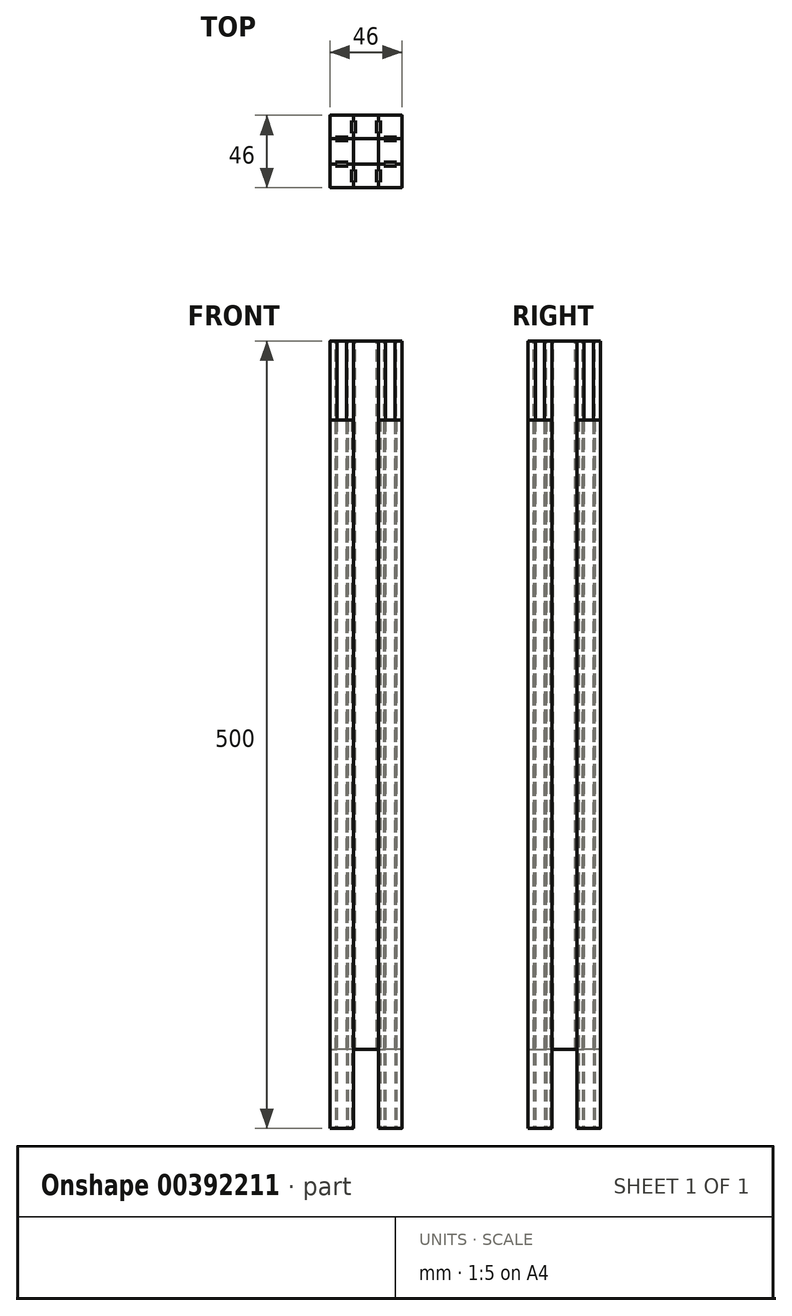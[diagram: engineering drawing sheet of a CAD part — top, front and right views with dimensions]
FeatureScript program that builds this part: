
annotation { "Feature Type Name" : "Feature", "Feature Type Description" : "" }
export const myFeature = defineFeature(function(context is Context, id is Id, definition is map)
    precondition{}
    {
        {
            var Q0;
            Q0=qCreatedBy(makeId("Top.planeOp"),FACE);
            var sketch = newSketch(context, id + "F0", { "sketchPlane" : qUnion([Q0])});
            skLineSegment(sketch, "E0.bottom", {"start": v(8, -8) * mm, "end": v(-8, -8) * mm});
            skLineSegment(sketch, "E0.top", {"start": v(8, 8) * mm, "end": v(-8, 8) * mm});
            skLineSegment(sketch, "E0.left", {"start": v(8, -8) * mm, "end": v(8, 8) * mm});
            skLineSegment(sketch, "E0.right", {"start": v(-8, -8) * mm, "end": v(-8, 8) * mm});
            skPoint(sketch, "E0.middle", {"position": v(0, 0) * mm});
            skSolve(sketch);
        }
        {
            var Q0;
            Q0=qCreatedBy(makeId("Top.planeOp"),FACE);
            cPlane(context, id + "F1", {"entities" : qUnion([Q0]), "cplaneType" : CPlaneType.OFFSET, "offset" : 500 * mm, "width" : 150 * mm, "height" : 150 * mm});
        }
        {
            var Q0;
            Q0=qCreatedBy(makeId("Top.planeOp"),FACE);
            var sketch = newSketch(context, id + "F2", { "sketchPlane" : qUnion([Q0])});
            skLineSegment(sketch, "E1.top", {"start": v(-8.5, -23) * mm, "end": v(-22.5, -23) * mm});
            skLineSegment(sketch, "E1.right", {"start": v(-23, -8.5) * mm, "end": v(-23, -22.5) * mm});
            skPoint(sketch, "E2", {"position": v(-15.5, -8) * mm});
            skLineSegment(sketch, "E3", {"start": v(-22.5, -8) * mm, "end": v(-18.5, -8) * mm});
            skLineSegment(sketch, "E4", {"start": v(-18.5, -8) * mm, "end": v(-19.5, -9.2) * mm});
            skLineSegment(sketch, "E5", {"start": v(-19.5, -9.2) * mm, "end": v(-15.5, -9.2) * mm});
            skLineSegment(sketch, "E6", {"start": v(-15.5, -9.2) * mm, "end": v(-15.5, -8) * mm, "construction": true});
            skLineSegment(sketch, "E7.MirrorCS", {"start": v(-11.5, -9.2) * mm, "end": v(-15.5, -9.2) * mm});
            skLineSegment(sketch, "E8.MirrorCS", {"start": v(-8.5, -8) * mm, "end": v(-12.5, -8) * mm});
            skLineSegment(sketch, "E9.MirrorCS", {"start": v(-12.5, -8) * mm, "end": v(-11.5, -9.2) * mm});
            skLineSegment(sketch, "E10", {"start": v(-8, -8) * mm, "end": v(-23, -23) * mm, "construction": true});
            skLineSegment(sketch, "E11.MirrorCS", {"start": v(-8, -8.5) * mm, "end": v(-8, -12.5) * mm});
            skLineSegment(sketch, "E12.MirrorCS", {"start": v(-8, -12.5) * mm, "end": v(-9.2, -11.5) * mm});
            skLineSegment(sketch, "E13.MirrorCS", {"start": v(-9.2, -11.5) * mm, "end": v(-9.2, -15.5) * mm});
            skLineSegment(sketch, "E14.MirrorCS", {"start": v(-9.2, -19.5) * mm, "end": v(-9.2, -15.5) * mm});
            skLineSegment(sketch, "E15.MirrorCS", {"start": v(-8, -22.5) * mm, "end": v(-8, -18.5) * mm});
            skLineSegment(sketch, "E16.MirrorCS", {"start": v(-8, -18.5) * mm, "end": v(-9.2, -19.5) * mm});
            skPoint(sketch, "E17.center", {"position": v(0, 0) * mm});
            skPoint(sketch, "E18.visualSharp", {"position": v(-23, -8) * mm});
            skArc(sketch, "E18.filletArc", {"start": v(-22.5, -8) * mm, "mid": v(-22.85, -8.15) * mm, "end": v(-23, -8.5) * mm});
            skPoint(sketch, "E19.visualSharp", {"position": v(-8, -8) * mm});
            skArc(sketch, "E19.filletArc", {"start": v(-8, -8.5) * mm, "mid": v(-8.15, -8.15) * mm, "end": v(-8.5, -8) * mm});
            skArc(sketch, "E20.filletArc", {"start": v(-8.5, -23) * mm, "mid": v(-8.15, -22.85) * mm, "end": v(-8, -22.5) * mm});
            skPoint(sketch, "E21.visualSharp", {"position": v(-23, -23) * mm});
            skArc(sketch, "E21.filletArc", {"start": v(-23, -22.5) * mm, "mid": v(-22.85, -22.85) * mm, "end": v(-22.5, -23) * mm});
            skLineSegment(sketch, "E22.1.0", {"start": v(8.5, -23) * mm, "end": v(22.5, -23) * mm});
            skLineSegment(sketch, "E22.1.1", {"start": v(23, -8.5) * mm, "end": v(23, -22.5) * mm});
            skLineSegment(sketch, "E22.1.2", {"start": v(8, -8) * mm, "end": v(23, -23) * mm, "construction": true});
            skPoint(sketch, "E22.1.3", {"position": v(8, -15.5) * mm});
            skPoint(sketch, "E22.1.4", {"position": v(8, -8) * mm});
            skPoint(sketch, "E22.1.5", {"position": v(23, -23) * mm});
            skPoint(sketch, "E22.1.6", {"position": v(8, -23) * mm});
            skLineSegment(sketch, "E22.1.7", {"start": v(18.5, -8) * mm, "end": v(19.5, -9.2) * mm});
            skLineSegment(sketch, "E22.1.8", {"start": v(9.2, -11.5) * mm, "end": v(9.2, -15.5) * mm});
            skLineSegment(sketch, "E22.1.9", {"start": v(22.5, -8) * mm, "end": v(18.5, -8) * mm});
            skLineSegment(sketch, "E22.1.10", {"start": v(19.5, -9.2) * mm, "end": v(15.5, -9.2) * mm});
            skLineSegment(sketch, "E22.1.11", {"start": v(8, -8.5) * mm, "end": v(8, -12.5) * mm});
            skLineSegment(sketch, "E22.1.12", {"start": v(12.5, -8) * mm, "end": v(11.5, -9.2) * mm});
            skLineSegment(sketch, "E22.1.13", {"start": v(8.5, -8) * mm, "end": v(12.5, -8) * mm});
            skLineSegment(sketch, "E22.1.14", {"start": v(11.5, -9.2) * mm, "end": v(15.5, -9.2) * mm});
            skLineSegment(sketch, "E22.1.15", {"start": v(8, -12.5) * mm, "end": v(9.2, -11.5) * mm});
            skLineSegment(sketch, "E22.1.16", {"start": v(9.2, -19.5) * mm, "end": v(9.2, -15.5) * mm});
            skLineSegment(sketch, "E22.1.17", {"start": v(9.2, -15.5) * mm, "end": v(8, -15.5) * mm, "construction": true});
            skLineSegment(sketch, "E22.1.18", {"start": v(8, -22.5) * mm, "end": v(8, -18.5) * mm});
            skLineSegment(sketch, "E22.1.19", {"start": v(8, -18.5) * mm, "end": v(9.2, -19.5) * mm});
            skArc(sketch, "E22.1.20", {"start": v(8, -22.5) * mm, "mid": v(8.15, -22.85) * mm, "end": v(8.5, -23) * mm});
            skArc(sketch, "E22.1.21", {"start": v(23, -8.5) * mm, "mid": v(22.85, -8.15) * mm, "end": v(22.5, -8) * mm});
            skArc(sketch, "E22.1.22", {"start": v(8.5, -8) * mm, "mid": v(8.15, -8.15) * mm, "end": v(8, -8.5) * mm});
            skArc(sketch, "E22.1.23", {"start": v(22.5, -23) * mm, "mid": v(22.85, -22.85) * mm, "end": v(23, -22.5) * mm});
            skLineSegment(sketch, "E22.2.0", {"start": v(23, 8.5) * mm, "end": v(23, 22.5) * mm});
            skLineSegment(sketch, "E22.2.1", {"start": v(8.5, 23) * mm, "end": v(22.5, 23) * mm});
            skLineSegment(sketch, "E22.2.2", {"start": v(8, 8) * mm, "end": v(23, 23) * mm, "construction": true});
            skPoint(sketch, "E22.2.3", {"position": v(15.5, 8) * mm});
            skPoint(sketch, "E22.2.4", {"position": v(8, 8) * mm});
            skPoint(sketch, "E22.2.5", {"position": v(23, 23) * mm});
            skPoint(sketch, "E22.2.6", {"position": v(23, 8) * mm});
            skLineSegment(sketch, "E22.2.7", {"start": v(8, 18.5) * mm, "end": v(9.2, 19.5) * mm});
            skLineSegment(sketch, "E22.2.8", {"start": v(11.5, 9.2) * mm, "end": v(15.5, 9.2) * mm});
            skLineSegment(sketch, "E22.2.9", {"start": v(8, 22.5) * mm, "end": v(8, 18.5) * mm});
            skLineSegment(sketch, "E22.2.10", {"start": v(9.2, 19.5) * mm, "end": v(9.2, 15.5) * mm});
            skLineSegment(sketch, "E22.2.11", {"start": v(8.5, 8) * mm, "end": v(12.5, 8) * mm});
            skLineSegment(sketch, "E22.2.12", {"start": v(8, 12.5) * mm, "end": v(9.2, 11.5) * mm});
            skLineSegment(sketch, "E22.2.13", {"start": v(8, 8.5) * mm, "end": v(8, 12.5) * mm});
            skLineSegment(sketch, "E22.2.14", {"start": v(9.2, 11.5) * mm, "end": v(9.2, 15.5) * mm});
            skLineSegment(sketch, "E22.2.15", {"start": v(12.5, 8) * mm, "end": v(11.5, 9.2) * mm});
            skLineSegment(sketch, "E22.2.16", {"start": v(19.5, 9.2) * mm, "end": v(15.5, 9.2) * mm});
            skLineSegment(sketch, "E22.2.17", {"start": v(15.5, 9.2) * mm, "end": v(15.5, 8) * mm, "construction": true});
            skLineSegment(sketch, "E22.2.18", {"start": v(22.5, 8) * mm, "end": v(18.5, 8) * mm});
            skLineSegment(sketch, "E22.2.19", {"start": v(18.5, 8) * mm, "end": v(19.5, 9.2) * mm});
            skArc(sketch, "E22.2.20", {"start": v(22.5, 8) * mm, "mid": v(22.85, 8.15) * mm, "end": v(23, 8.5) * mm});
            skArc(sketch, "E22.2.21", {"start": v(8.5, 23) * mm, "mid": v(8.15, 22.85) * mm, "end": v(8, 22.5) * mm});
            skArc(sketch, "E22.2.22", {"start": v(8, 8.5) * mm, "mid": v(8.15, 8.15) * mm, "end": v(8.5, 8) * mm});
            skArc(sketch, "E22.2.23", {"start": v(23, 22.5) * mm, "mid": v(22.85, 22.85) * mm, "end": v(22.5, 23) * mm});
            skLineSegment(sketch, "E22.3.0", {"start": v(-8.5, 23) * mm, "end": v(-22.5, 23) * mm});
            skLineSegment(sketch, "E22.3.1", {"start": v(-23, 8.5) * mm, "end": v(-23, 22.5) * mm});
            skLineSegment(sketch, "E22.3.2", {"start": v(-8, 8) * mm, "end": v(-23, 23) * mm, "construction": true});
            skPoint(sketch, "E22.3.3", {"position": v(-8, 15.5) * mm});
            skPoint(sketch, "E22.3.4", {"position": v(-8, 8) * mm});
            skPoint(sketch, "E22.3.5", {"position": v(-23, 23) * mm});
            skPoint(sketch, "E22.3.6", {"position": v(-8, 23) * mm});
            skLineSegment(sketch, "E22.3.7", {"start": v(-18.5, 8) * mm, "end": v(-19.5, 9.2) * mm});
            skLineSegment(sketch, "E22.3.8", {"start": v(-9.2, 11.5) * mm, "end": v(-9.2, 15.5) * mm});
            skLineSegment(sketch, "E22.3.9", {"start": v(-22.5, 8) * mm, "end": v(-18.5, 8) * mm});
            skLineSegment(sketch, "E22.3.10", {"start": v(-19.5, 9.2) * mm, "end": v(-15.5, 9.2) * mm});
            skLineSegment(sketch, "E22.3.11", {"start": v(-8, 8.5) * mm, "end": v(-8, 12.5) * mm});
            skLineSegment(sketch, "E22.3.12", {"start": v(-12.5, 8) * mm, "end": v(-11.5, 9.2) * mm});
            skLineSegment(sketch, "E22.3.13", {"start": v(-8.5, 8) * mm, "end": v(-12.5, 8) * mm});
            skLineSegment(sketch, "E22.3.14", {"start": v(-11.5, 9.2) * mm, "end": v(-15.5, 9.2) * mm});
            skLineSegment(sketch, "E22.3.15", {"start": v(-8, 12.5) * mm, "end": v(-9.2, 11.5) * mm});
            skLineSegment(sketch, "E22.3.16", {"start": v(-9.2, 19.5) * mm, "end": v(-9.2, 15.5) * mm});
            skLineSegment(sketch, "E22.3.17", {"start": v(-9.2, 15.5) * mm, "end": v(-8, 15.5) * mm, "construction": true});
            skLineSegment(sketch, "E22.3.18", {"start": v(-8, 22.5) * mm, "end": v(-8, 18.5) * mm});
            skLineSegment(sketch, "E22.3.19", {"start": v(-8, 18.5) * mm, "end": v(-9.2, 19.5) * mm});
            skArc(sketch, "E22.3.20", {"start": v(-8, 22.5) * mm, "mid": v(-8.15, 22.85) * mm, "end": v(-8.5, 23) * mm});
            skArc(sketch, "E22.3.21", {"start": v(-23, 8.5) * mm, "mid": v(-22.85, 8.15) * mm, "end": v(-22.5, 8) * mm});
            skArc(sketch, "E22.3.22", {"start": v(-8.5, 8) * mm, "mid": v(-8.15, 8.15) * mm, "end": v(-8, 8.5) * mm});
            skArc(sketch, "E22.3.23", {"start": v(-22.5, 23) * mm, "mid": v(-22.85, 22.85) * mm, "end": v(-23, 22.5) * mm});
            skSolve(sketch);
        }
        {
            var Q0;
            Q0=qCreatedBy(id+"F1.planeOp",FACE);
            var sketch = newSketch(context, id + "F3", { "sketchPlane" : qUnion([Q0])});
            skArc(sketch, "E23.0", {"start": v(-23, 8.5) * mm, "mid": v(-22.85, 8.15) * mm, "end": v(-22.5, 8) * mm, "construction": true});
            skLineSegment(sketch, "E23.1", {"start": v(-22.5, 8) * mm, "end": v(-18.5, 8) * mm});
            skLineSegment(sketch, "E23.2", {"start": v(-18.5, 8) * mm, "end": v(-19.5, 9.2) * mm, "construction": true});
            skLineSegment(sketch, "E23.3", {"start": v(-19.5, 9.2) * mm, "end": v(-15.5, 9.2) * mm, "construction": true});
            skLineSegment(sketch, "E23.4", {"start": v(-11.5, 9.2) * mm, "end": v(-15.5, 9.2) * mm, "construction": true});
            skLineSegment(sketch, "E23.5", {"start": v(-12.5, 8) * mm, "end": v(-11.5, 9.2) * mm, "construction": true});
            skLineSegment(sketch, "E23.6", {"start": v(-8.5, 8) * mm, "end": v(-12.5, 8) * mm});
            skArc(sketch, "E23.7", {"start": v(-8.5, 8) * mm, "mid": v(-8.15, 8.15) * mm, "end": v(-8, 8.5) * mm, "construction": true});
            skArc(sketch, "E24.MirrorCS", {"start": v(-8.5, 8) * mm, "mid": v(-8.15, 7.85) * mm, "end": v(-8, 7.5) * mm});
            skArc(sketch, "E25.MirrorCS", {"start": v(-23, 7.5) * mm, "mid": v(-22.85, 7.85) * mm, "end": v(-22.5, 8) * mm});
            skLineSegment(sketch, "E26.MirrorCS", {"start": v(-12.5, 8) * mm, "end": v(-11.5, 6.8) * mm});
            skLineSegment(sketch, "E27.MirrorCS", {"start": v(-11.5, 6.8) * mm, "end": v(-15.5, 6.8) * mm});
            skLineSegment(sketch, "E28.MirrorCS", {"start": v(-18.5, 8) * mm, "end": v(-19.5, 6.8) * mm});
            skLineSegment(sketch, "E29.MirrorCS", {"start": v(-19.5, 6.8) * mm, "end": v(-15.5, 6.8) * mm});
            skLineSegment(sketch, "E30", {"start": v(-8, 0) * mm, "end": v(-8, 7.5) * mm});
            skLineSegment(sketch, "E31", {"start": v(-23, 7.5) * mm, "end": v(-23, 0) * mm});
            skLineSegment(sketch, "E32", {"start": v(-23, 0) * mm, "end": v(-8, 0) * mm, "construction": true});
            skLineSegment(sketch, "E33.MirrorCS", {"start": v(-8, 0) * mm, "end": v(-8, -7.5) * mm});
            skArc(sketch, "E34.MirrorCS", {"start": v(-8.5, -8) * mm, "mid": v(-8.15, -7.85) * mm, "end": v(-8, -7.5) * mm});
            skLineSegment(sketch, "E35.MirrorCS", {"start": v(-8.5, -8) * mm, "end": v(-12.5, -8) * mm});
            skLineSegment(sketch, "E36.MirrorCS", {"start": v(-12.5, -8) * mm, "end": v(-11.5, -6.8) * mm});
            skLineSegment(sketch, "E37.MirrorCS", {"start": v(-11.5, -6.8) * mm, "end": v(-15.5, -6.8) * mm});
            skLineSegment(sketch, "E38.MirrorCS", {"start": v(-19.5, -6.8) * mm, "end": v(-15.5, -6.8) * mm});
            skLineSegment(sketch, "E39.MirrorCS", {"start": v(-18.5, -8) * mm, "end": v(-19.5, -6.8) * mm});
            skLineSegment(sketch, "E40.MirrorCS", {"start": v(-23, -7.5) * mm, "end": v(-23, 0) * mm});
            skLineSegment(sketch, "E41.MirrorCS", {"start": v(-22.5, -8) * mm, "end": v(-18.5, -8) * mm});
            skArc(sketch, "E42.MirrorCS", {"start": v(-23, -7.5) * mm, "mid": v(-22.85, -7.85) * mm, "end": v(-22.5, -8) * mm});
            skLineSegment(sketch, "E43.1.0", {"start": v(0, -23) * mm, "end": v(0, -8) * mm, "construction": true});
            skLineSegment(sketch, "E43.1.1", {"start": v(8, -8.5) * mm, "end": v(8, -12.5) * mm});
            skLineSegment(sketch, "E43.1.2", {"start": v(-8, -8.5) * mm, "end": v(-8, -12.5) * mm});
            skLineSegment(sketch, "E43.1.3", {"start": v(7.5, -23) * mm, "end": v(0, -23) * mm});
            skLineSegment(sketch, "E43.1.4", {"start": v(6.8, -19.5) * mm, "end": v(6.8, -15.5) * mm});
            skLineSegment(sketch, "E43.1.5", {"start": v(6.8, -11.5) * mm, "end": v(6.8, -15.5) * mm});
            skLineSegment(sketch, "E43.1.6", {"start": v(0, -8) * mm, "end": v(-7.5, -8) * mm});
            skLineSegment(sketch, "E43.1.7", {"start": v(-6.8, -19.5) * mm, "end": v(-6.8, -15.5) * mm});
            skLineSegment(sketch, "E43.1.8", {"start": v(0, -8) * mm, "end": v(7.5, -8) * mm});
            skLineSegment(sketch, "E43.1.9", {"start": v(-7.5, -23) * mm, "end": v(0, -23) * mm});
            skLineSegment(sketch, "E43.1.10", {"start": v(-6.8, -11.5) * mm, "end": v(-6.8, -15.5) * mm});
            skLineSegment(sketch, "E43.1.11", {"start": v(8, -22.5) * mm, "end": v(8, -18.5) * mm});
            skLineSegment(sketch, "E43.1.12", {"start": v(-8, -22.5) * mm, "end": v(-8, -18.5) * mm});
            skLineSegment(sketch, "E43.1.13", {"start": v(8, -18.5) * mm, "end": v(6.8, -19.5) * mm});
            skLineSegment(sketch, "E43.1.14", {"start": v(8, -12.5) * mm, "end": v(6.8, -11.5) * mm});
            skArc(sketch, "E43.1.15", {"start": v(-8, -8.5) * mm, "mid": v(-7.85, -8.15) * mm, "end": v(-7.5, -8) * mm});
            skLineSegment(sketch, "E43.1.16", {"start": v(-8, -12.5) * mm, "end": v(-6.8, -11.5) * mm});
            skArc(sketch, "E43.1.17", {"start": v(-7.5, -23) * mm, "mid": v(-7.85, -22.85) * mm, "end": v(-8, -22.5) * mm});
            skLineSegment(sketch, "E43.1.18", {"start": v(-8, -18.5) * mm, "end": v(-6.8, -19.5) * mm});
            skArc(sketch, "E43.1.19", {"start": v(7.5, -23) * mm, "mid": v(7.85, -22.85) * mm, "end": v(8, -22.5) * mm});
            skArc(sketch, "E43.1.20", {"start": v(8, -8.5) * mm, "mid": v(7.85, -8.15) * mm, "end": v(7.5, -8) * mm});
            skLineSegment(sketch, "E43.2.0", {"start": v(23, 0) * mm, "end": v(8, 0) * mm, "construction": true});
            skLineSegment(sketch, "E43.2.1", {"start": v(8.5, 8) * mm, "end": v(12.5, 8) * mm});
            skLineSegment(sketch, "E43.2.2", {"start": v(8.5, -8) * mm, "end": v(12.5, -8) * mm});
            skLineSegment(sketch, "E43.2.3", {"start": v(23, 7.5) * mm, "end": v(23, 0) * mm});
            skLineSegment(sketch, "E43.2.4", {"start": v(19.5, 6.8) * mm, "end": v(15.5, 6.8) * mm});
            skLineSegment(sketch, "E43.2.5", {"start": v(11.5, 6.8) * mm, "end": v(15.5, 6.8) * mm});
            skLineSegment(sketch, "E43.2.6", {"start": v(8, 0) * mm, "end": v(8, -7.5) * mm});
            skLineSegment(sketch, "E43.2.7", {"start": v(19.5, -6.8) * mm, "end": v(15.5, -6.8) * mm});
            skLineSegment(sketch, "E43.2.8", {"start": v(8, 0) * mm, "end": v(8, 7.5) * mm});
            skLineSegment(sketch, "E43.2.9", {"start": v(23, -7.5) * mm, "end": v(23, 0) * mm});
            skLineSegment(sketch, "E43.2.10", {"start": v(11.5, -6.8) * mm, "end": v(15.5, -6.8) * mm});
            skLineSegment(sketch, "E43.2.11", {"start": v(22.5, 8) * mm, "end": v(18.5, 8) * mm});
            skLineSegment(sketch, "E43.2.12", {"start": v(22.5, -8) * mm, "end": v(18.5, -8) * mm});
            skLineSegment(sketch, "E43.2.13", {"start": v(18.5, 8) * mm, "end": v(19.5, 6.8) * mm});
            skLineSegment(sketch, "E43.2.14", {"start": v(12.5, 8) * mm, "end": v(11.5, 6.8) * mm});
            skArc(sketch, "E43.2.15", {"start": v(8.5, -8) * mm, "mid": v(8.15, -7.85) * mm, "end": v(8, -7.5) * mm});
            skLineSegment(sketch, "E43.2.16", {"start": v(12.5, -8) * mm, "end": v(11.5, -6.8) * mm});
            skArc(sketch, "E43.2.17", {"start": v(23, -7.5) * mm, "mid": v(22.85, -7.85) * mm, "end": v(22.5, -8) * mm});
            skLineSegment(sketch, "E43.2.18", {"start": v(18.5, -8) * mm, "end": v(19.5, -6.8) * mm});
            skArc(sketch, "E43.2.19", {"start": v(23, 7.5) * mm, "mid": v(22.85, 7.85) * mm, "end": v(22.5, 8) * mm});
            skArc(sketch, "E43.2.20", {"start": v(8.5, 8) * mm, "mid": v(8.15, 7.85) * mm, "end": v(8, 7.5) * mm});
            skLineSegment(sketch, "E43.3.0", {"start": v(0, 23) * mm, "end": v(0, 8) * mm, "construction": true});
            skLineSegment(sketch, "E43.3.1", {"start": v(-8, 8.5) * mm, "end": v(-8, 12.5) * mm});
            skLineSegment(sketch, "E43.3.2", {"start": v(8, 8.5) * mm, "end": v(8, 12.5) * mm});
            skLineSegment(sketch, "E43.3.3", {"start": v(-7.5, 23) * mm, "end": v(0, 23) * mm});
            skLineSegment(sketch, "E43.3.4", {"start": v(-6.8, 19.5) * mm, "end": v(-6.8, 15.5) * mm});
            skLineSegment(sketch, "E43.3.5", {"start": v(-6.8, 11.5) * mm, "end": v(-6.8, 15.5) * mm});
            skLineSegment(sketch, "E43.3.6", {"start": v(0, 8) * mm, "end": v(7.5, 8) * mm});
            skLineSegment(sketch, "E43.3.7", {"start": v(6.8, 19.5) * mm, "end": v(6.8, 15.5) * mm});
            skLineSegment(sketch, "E43.3.8", {"start": v(0, 8) * mm, "end": v(-7.5, 8) * mm});
            skLineSegment(sketch, "E43.3.9", {"start": v(7.5, 23) * mm, "end": v(0, 23) * mm});
            skLineSegment(sketch, "E43.3.10", {"start": v(6.8, 11.5) * mm, "end": v(6.8, 15.5) * mm});
            skLineSegment(sketch, "E43.3.11", {"start": v(-8, 22.5) * mm, "end": v(-8, 18.5) * mm});
            skLineSegment(sketch, "E43.3.12", {"start": v(8, 22.5) * mm, "end": v(8, 18.5) * mm});
            skLineSegment(sketch, "E43.3.13", {"start": v(-8, 18.5) * mm, "end": v(-6.8, 19.5) * mm});
            skLineSegment(sketch, "E43.3.14", {"start": v(-8, 12.5) * mm, "end": v(-6.8, 11.5) * mm});
            skArc(sketch, "E43.3.15", {"start": v(8, 8.5) * mm, "mid": v(7.85, 8.15) * mm, "end": v(7.5, 8) * mm});
            skLineSegment(sketch, "E43.3.16", {"start": v(8, 12.5) * mm, "end": v(6.8, 11.5) * mm});
            skArc(sketch, "E43.3.17", {"start": v(7.5, 23) * mm, "mid": v(7.85, 22.85) * mm, "end": v(8, 22.5) * mm});
            skLineSegment(sketch, "E43.3.18", {"start": v(8, 18.5) * mm, "end": v(6.8, 19.5) * mm});
            skArc(sketch, "E43.3.19", {"start": v(-7.5, 23) * mm, "mid": v(-7.85, 22.85) * mm, "end": v(-8, 22.5) * mm});
            skArc(sketch, "E43.3.20", {"start": v(-8, 8.5) * mm, "mid": v(-7.85, 8.15) * mm, "end": v(-7.5, 8) * mm});
            skPoint(sketch, "E43.center", {"position": v(0, 0) * mm});
            skSolve(sketch);
        }
        {
            var Q0;
            Q0 = qSketchRegion(id + "F2", true);
            extrude(context, id + "F4", {"entities" : qUnion([Q0]), "depth" : 450 * mm});
        }
        {
            var Q0;
            Q0 = qSketchRegion(id + "F3", true);
            extrude(context, id + "F5", {"entities" : qUnion([Q0]), "oppositeDirection" : true, "depth" : 450 * mm});
        }
    });
